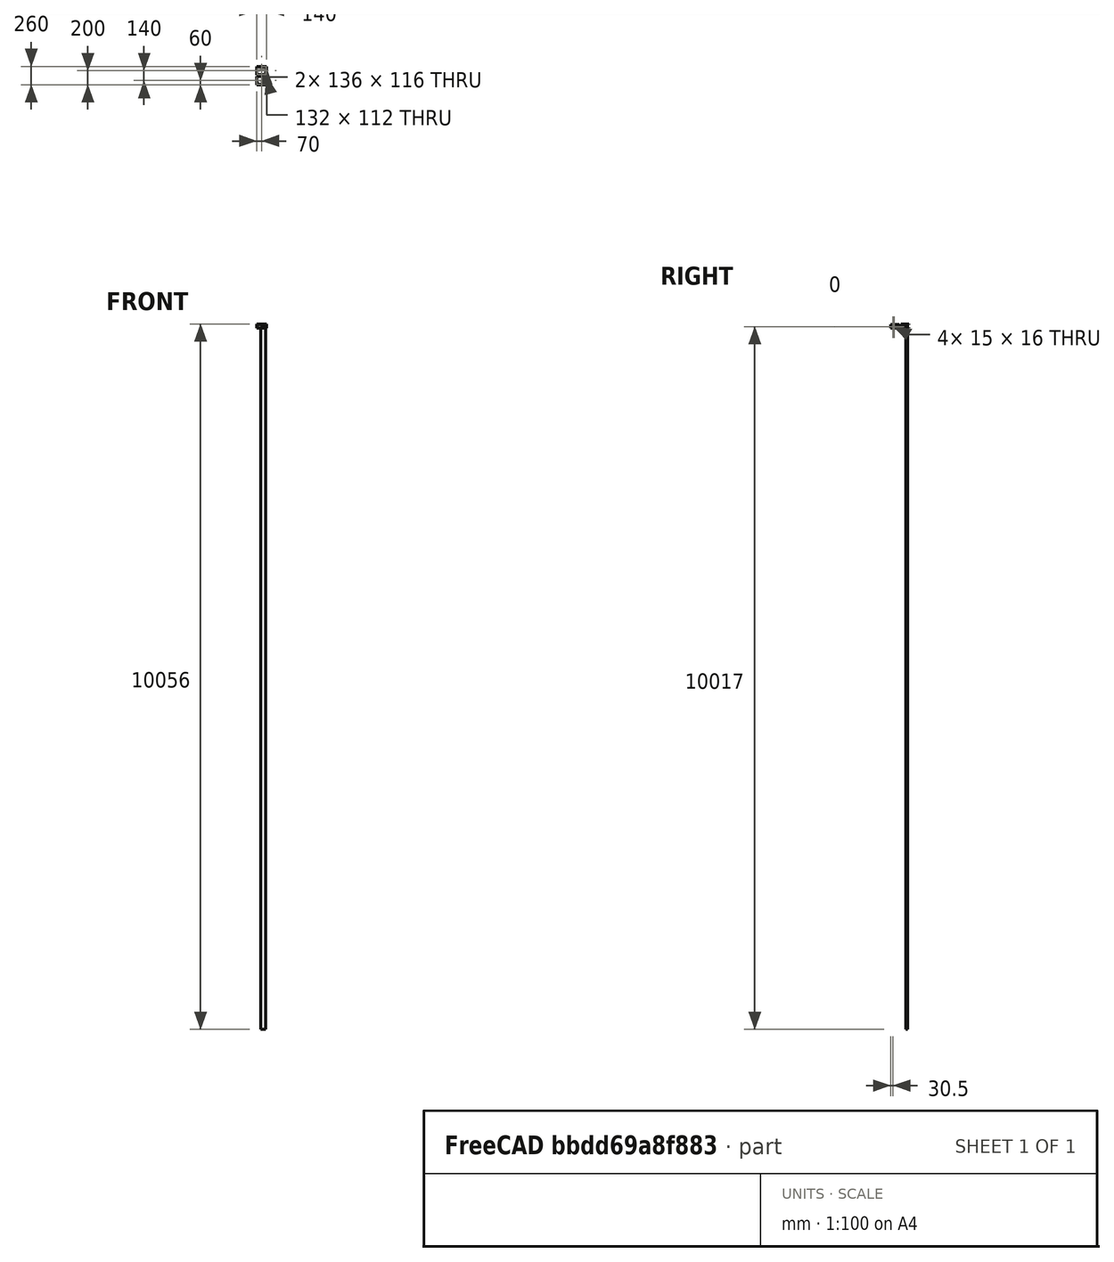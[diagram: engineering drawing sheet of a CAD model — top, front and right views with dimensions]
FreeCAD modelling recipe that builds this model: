
FCSTD DOCUMENT  (FreeCAD 0.15R4671 (Git))
Label: receptor
License: All rights reserved
LicenseURL: http://en.wikipedia.org/wiki/All_rights_reserved
objects: Sketcher::SketchObject×18, PartDesign::Pocket×11, PartDesign::Pad×7
note: 54 computed .brp shape members not serialized (recipe doc carries the construction recipe); baked Part::Feature solids carry a one-line shape summary decoded from their .brp

FEATURE [Sketcher::SketchObject] Sketch  label="full filled box"
  sketch-geometry (4):
    g0: LineSegment StartX=-70 StartY=60 StartZ=0 EndX=70 EndY=60 EndZ=0
    g1: LineSegment StartX=70 StartY=60 StartZ=0 EndX=70 EndY=-60 EndZ=0
    g2: LineSegment StartX=70 StartY=-60 StartZ=0 EndX=-70 EndY=-60 EndZ=0
    g3: LineSegment StartX=-70 StartY=-60 StartZ=0 EndX=-70 EndY=60 EndZ=0
  constraints (12):
    c: Coincident(g0,g1)
    c: Coincident(g1,g2)
    c: Coincident(g2,g3)
    c: Coincident(g3,g0)
    c: Horizontal(g0)
    c: Horizontal(g2)
    c: Vertical(g1)
    c: Vertical(g3)
    c: Symmetric(g0,g2,g-1)
    c: Symmetric(g0,g0,g-2)
    c: DistanceX(g0) = 140
    c: DistanceY(g3) = 120
FEATURE [PartDesign::Pad] Pad  label="full filled box001"
  Length = 50
  Length2 = 100
  Sketch = -> Sketch
  Type = 0
FEATURE [Sketcher::SketchObject] Sketch001  label="main hole box"
  Placement = pos=(0,0,50) rot=(0,0,1;0rad)
  Support = -> Pad [Face6]
  sketch-geometry (4):
    g0: LineSegment StartX=-68 StartY=58 StartZ=0 EndX=68 EndY=58 EndZ=0
    g1: LineSegment StartX=68 StartY=58 StartZ=0 EndX=68 EndY=-58 EndZ=0
    g2: LineSegment StartX=68 StartY=-58 StartZ=0 EndX=-68 EndY=-58 EndZ=0
    g3: LineSegment StartX=-68 StartY=-58 StartZ=0 EndX=-68 EndY=58 EndZ=0
  constraints (12):
    c: Coincident(g0,g1)
    c: Coincident(g1,g2)
    c: Coincident(g2,g3)
    c: Coincident(g3,g0)
    c: Horizontal(g0)
    c: Horizontal(g2)
    c: Vertical(g1)
    c: Vertical(g3)
    c: Symmetric(g0,g0,g-2)
    c: Symmetric(g0,g2,g-1)
    c: DistanceX(g0) = 136
    c: DistanceY(g3) = 116
FEATURE [PartDesign::Pocket] Pocket  label="main hole box001"
  Length = 48
  Sketch = -> Sketch001
  Type = 0
FEATURE [Sketcher::SketchObject] Sketch002
  Placement = pos=(0,0,2) rot=(0,0,1;0rad)
  Support = -> Pocket [Face11]
  sketch-geometry (8):
    g0: Circle CenterX=44 CenterY=-55 CenterZ=0 NormalX=0 NormalY=0 NormalZ=1 Radius=3
    g1: Circle CenterX=-14 CenterY=-55 CenterZ=0 NormalX=0 NormalY=0 NormalZ=1 Radius=3
    g2: Circle CenterX=44 CenterY=-6.5 CenterZ=0 NormalX=0 NormalY=0 NormalZ=1 Radius=3
    g3: Circle CenterX=-14 CenterY=-6.5 CenterZ=0 NormalX=0 NormalY=0 NormalZ=1 Radius=3
    g4: LineSegment [constr] StartX=-14 StartY=-6.5 StartZ=0 EndX=44 EndY=-6.5 EndZ=0
    g5: LineSegment [constr] StartX=-14 StartY=-6.5 StartZ=0 EndX=-14 EndY=-55 EndZ=0
    g6: LineSegment [constr] StartX=-14 StartY=-55 StartZ=0 EndX=44 EndY=-55 EndZ=0
    g7: LineSegment [constr] StartX=44 StartY=-6.5 StartZ=0 EndX=44 EndY=-55 EndZ=0
  constraints (20):
    c: Radius(g3) = 3
    c: Radius(g2) = 3
    c: Radius(g1) = 3
    c: Radius(g0) = 3
    c: DistanceY(g-1,g0) = -55
    c: DistanceX(g1,g0) = 58
    c: DistanceY(g0,g2) = 48.5
    c: DistanceX(g-1,g2) = 44
    c: Coincident(g4,g3)
    c: Coincident(g4,g2)
    c: Horizontal(g4)
    c: Coincident(g5,g3)
    c: Coincident(g5,g1)
    c: Vertical(g5)
    c: Coincident(g6,g1)
    c: Coincident(g6,g0)
    c: Coincident(g7,g2)
    c: Coincident(g7,g0)
    c: Vertical(g7)
    c: Horizontal(g6)
FEATURE [PartDesign::Pad] Pad001  label="legs raspberry fill"
  Length = 8
  Length2 = 100
  Sketch = -> Sketch002
  Type = 0
FEATURE [Sketcher::SketchObject] Sketch003
  Placement = pos=(0,0,10) rot=(0,0,1;0rad)
  Support = -> Pad001 [Face18]
  sketch-geometry (8):
    g0: Circle CenterX=-14 CenterY=-6.5 CenterZ=0 NormalX=0 NormalY=0 NormalZ=1 Radius=1.1
    g1: Circle CenterX=44 CenterY=-6.5 CenterZ=0 NormalX=0 NormalY=0 NormalZ=1 Radius=1.1
    g2: Circle CenterX=-14 CenterY=-55 CenterZ=0 NormalX=0 NormalY=0 NormalZ=1 Radius=1.1
    g3: Circle CenterX=44 CenterY=-55 CenterZ=0 NormalX=0 NormalY=0 NormalZ=1 Radius=1.1
    g4: LineSegment [constr] StartX=-14 StartY=-6.5 StartZ=0 EndX=-14 EndY=-55 EndZ=0
    g5: LineSegment [constr] StartX=-14 StartY=-6.5 StartZ=0 EndX=44 EndY=-6.5 EndZ=0
    g6: LineSegment [constr] StartX=44 StartY=-6.5 StartZ=0 EndX=44 EndY=-55 EndZ=0
    g7: LineSegment [constr] StartX=44 StartY=-55 StartZ=0 EndX=-14 EndY=-55 EndZ=0
  constraints (20):
    c: Radius(g0) = 1.1
    c: Radius(g3) = 1.1
    c: Radius(g2) = 1.1
    c: Radius(g1) = 1.1
    c: Coincident(g4,g0)
    c: Coincident(g4,g2)
    c: Vertical(g4)
    c: Coincident(g5,g0)
    c: Horizontal(g5)
    c: Coincident(g1,g5)
    c: Coincident(g6,g1)
    c: Coincident(g6,g3)
    c: Vertical(g6)
    c: Coincident(g7,g3)
    c: Coincident(g7,g2)
    c: Horizontal(g7)
    c: DistanceY(g-1,g2) = -55
    c: DistanceX(g-1,g1) = 44
    c: DistanceY(g0,g2) = -48.5
    c: DistanceX(g0,g1) = 58
FEATURE [PartDesign::Pocket] Pocket001  label="legs raspberry hole"
  Length = 8
  Sketch = -> Sketch003
  Type = 0
FEATURE [Sketcher::SketchObject] Sketch004
  Placement = pos=(70,0,0) rot=(0.57735,0.57735,0.57735;2.0944rad)
  Support = -> Pocket001 [Face3]
  sketch-geometry (12):
    g0: LineSegment StartX=-56 StartY=25 StartZ=0 EndX=-40 EndY=25 EndZ=0
    g1: LineSegment StartX=-40 StartY=25 StartZ=0 EndX=-40 EndY=11 EndZ=0
    g2: LineSegment StartX=-40 StartY=11 StartZ=0 EndX=-56 EndY=11 EndZ=0
    g3: LineSegment StartX=-56 StartY=11 StartZ=0 EndX=-56 EndY=25 EndZ=0
    g4: LineSegment StartX=-37 StartY=27 StartZ=0 EndX=-22 EndY=27 EndZ=0
    g5: LineSegment StartX=-22 StartY=27 StartZ=0 EndX=-22 EndY=11 EndZ=0
    g6: LineSegment StartX=-22 StartY=11 StartZ=0 EndX=-37 EndY=11 EndZ=0
    g7: LineSegment StartX=-37 StartY=11 StartZ=0 EndX=-37 EndY=27 EndZ=0
    g8: LineSegment StartX=-19 StartY=27 StartZ=0 EndX=-4 EndY=27 EndZ=0
    g9: LineSegment StartX=-4 StartY=27 StartZ=0 EndX=-4 EndY=11 EndZ=0
    g10: LineSegment StartX=-4 StartY=11 StartZ=0 EndX=-19 EndY=11 EndZ=0
    g11: LineSegment StartX=-19 StartY=11 StartZ=0 EndX=-19 EndY=27 EndZ=0
  constraints (36):
    c: Coincident(g0,g1)
    c: Coincident(g1,g2)
    c: Coincident(g2,g3)
    c: Coincident(g3,g0)
    c: Horizontal(g0)
    c: Horizontal(g2)
    c: Vertical(g1)
    c: Vertical(g3)
    c: Coincident(g4,g5)
    c: Coincident(g5,g6)
    c: Coincident(g6,g7)
    c: Coincident(g7,g4)
    c: Horizontal(g4)
    c: Horizontal(g6)
    c: Vertical(g5)
    c: Vertical(g7)
    c: Coincident(g8,g9)
    c: Coincident(g9,g10)
    c: Coincident(g10,g11)
    c: Coincident(g11,g8)
    c: Horizontal(g8)
    c: Horizontal(g10)
    c: Vertical(g9)
    c: Vertical(g11)
    c: DistanceX(g-1,g2) = -56
    c: DistanceX(g2) = -16
    c: DistanceY(g3) = 14
    c: DistanceY(g-1,g1) = 11
    c: DistanceX(g6,g1) = -3
    c: DistanceY(g-1,g6) = 11
    c: DistanceY(g-1,g10) = 11
    c: DistanceX(g6) = -15
    c: DistanceY(g7) = 16
    c: DistanceY(g11) = 16
    c: DistanceX(g10) = -15
    c: DistanceX(g10,g5) = -3
FEATURE [PartDesign::Pocket] Pocket002  label="holes raspberry periphericals"
  Length = 5
  Sketch = -> Sketch004
  Type = 0
FEATURE [Sketcher::SketchObject] Sketch005
  Placement = pos=(0,-60,0) rot=(1,0,0;1.5708rad)
  Support = -> Pocket002 [Face6]
  sketch-geometry (9):
    g0: Circle CenterX=37 CenterY=14 CenterZ=0 NormalX=0 NormalY=0 NormalZ=1 Radius=3
    g1: LineSegment StartX=8 StartY=17 StartZ=0 EndX=23 EndY=17 EndZ=0
    g2: LineSegment StartX=23 StartY=17 StartZ=0 EndX=23 EndY=11 EndZ=0
    g3: LineSegment StartX=23 StartY=11 StartZ=0 EndX=8 EndY=11 EndZ=0
    g4: LineSegment StartX=8 StartY=11 StartZ=0 EndX=8 EndY=17 EndZ=0
    g5: LineSegment StartX=-10 StartY=14 StartZ=0 EndX=-2 EndY=14 EndZ=0
    g6: LineSegment StartX=-2 StartY=14 StartZ=0 EndX=-2 EndY=11 EndZ=0
    g7: LineSegment StartX=-2 StartY=11 StartZ=0 EndX=-10 EndY=11 EndZ=0
    g8: LineSegment StartX=-10 StartY=11 StartZ=0 EndX=-10 EndY=14 EndZ=0
  constraints (27):
    c: Coincident(g1,g2)
    c: Coincident(g2,g3)
    c: Coincident(g3,g4)
    c: Coincident(g4,g1)
    c: Horizontal(g1)
    c: Horizontal(g3)
    c: Vertical(g2)
    c: Vertical(g4)
    c: Coincident(g5,g6)
    c: Coincident(g6,g7)
    c: Coincident(g7,g8)
    c: Coincident(g8,g5)
    c: Horizontal(g5)
    c: Horizontal(g7)
    c: Vertical(g6)
    c: Vertical(g8)
    c: Radius(g0) = 3
    c: DistanceX(g1) = 15
    c: DistanceX(g5) = 8
    c: DistanceY(g8) = 3
    c: DistanceY(g4) = 6
    c: DistanceY(g-1,g6) = 11
    c: DistanceY(g-1,g2) = 11
    c: DistanceY(g-1,g0) = 14
    c: DistanceX(g-1,g7) = -10
    c: DistanceX(g6,g3) = 10
    c: DistanceX(g2,g0) = 14
FEATURE [PartDesign::Pocket] Pocket003  label="holes raspberry power"
  Length = 5
  Sketch = -> Sketch005
  Type = 0
FEATURE [Sketcher::SketchObject] Sketch006
  Placement = pos=(0,0,2) rot=(0,0,1;0rad)
  Support = -> Pocket003 [Face32]
  sketch-geometry (3):
    g0: Circle CenterX=-59 CenterY=-30 CenterZ=0 NormalX=0 NormalY=0 NormalZ=1 Radius=3
    g1: Circle CenterX=-46 CenterY=-30 CenterZ=0 NormalX=0 NormalY=0 NormalZ=1 Radius=3
    g2: LineSegment [constr] StartX=-59 StartY=-30 StartZ=0 EndX=-46 EndY=-30 EndZ=0
  constraints (8):
    c: Radius(g1) = 3
    c: Equal(g1,g0)
    c: Coincident(g2,g1)
    c: Coincident(g2,g0)
    c: Parallel(g2,g-1)
    c: DistanceX(g-1,g0) = -59
    c: DistanceX(g2) = 13
    c: DistanceY(g-1,g1) = -30
FEATURE [PartDesign::Pad] Pad002  label="legs lora fill"
  Length = 30
  Length2 = 100
  Sketch = -> Sketch006
  Type = 0
FEATURE [Sketcher::SketchObject] Sketch007
  Placement = pos=(0,0,32) rot=(0,0,1;0rad)
  Support = -> Pad002 [Face42]
  sketch-geometry (3):
    g0: Circle CenterX=-59 CenterY=-30 CenterZ=0 NormalX=0 NormalY=0 NormalZ=1 Radius=1.1
    g1: Circle CenterX=-46 CenterY=-30 CenterZ=0 NormalX=0 NormalY=0 NormalZ=1 Radius=1.1
    g2: LineSegment [constr] StartX=-59 StartY=-30 StartZ=0 EndX=-46 EndY=-30 EndZ=0
  constraints (8):
    c: Radius(g1) = 1.1
    c: Equal(g1,g0)
    c: Coincident(g2,g1)
    c: Parallel(g2,g-1)
    c: Coincident(g0,g2)
    c: DistanceX(g2) = 13
    c: DistanceX(g-1,g0) = -59
    c: DistanceY(g-1,g1) = -30
FEATURE [PartDesign::Pocket] Pocket004  label="legs lora hole"
  Length = 25
  Sketch = -> Sketch007
  Type = 0
FEATURE [Sketcher::SketchObject] Sketch008
  Placement = pos=(-70,0,0) rot=(0.57735,-0.57735,-0.57735;2.0944rad)
  Support = -> Pocket004 [Face2]
  sketch-geometry (1):
    g0: Circle CenterX=30 CenterY=38 CenterZ=0 NormalX=0 NormalY=0 NormalZ=1 Radius=4
  constraints (3):
    c: Radius(g0) = 4
    c: DistanceX(g-1,g0) = 30
    c: DistanceY(g-1,g0) = 38
FEATURE [PartDesign::Pocket] Pocket005  label="pocket lora antenna"
  Length = 5
  Sketch = -> Sketch008
  Type = 0
FEATURE [Sketcher::SketchObject] Sketch009  label="top 1"
  Placement = pos=(0,0,0) rot=(1,0,0;3.14159rad)
  Support = -> Pocket005 [Face4]
  sketch-geometry (4):
    g0: LineSegment StartX=-70 StartY=-80 StartZ=0 EndX=70 EndY=-80 EndZ=0
    g1: LineSegment StartX=70 StartY=-80 StartZ=0 EndX=70 EndY=-200 EndZ=0
    g2: LineSegment StartX=70 StartY=-200 StartZ=0 EndX=-70 EndY=-200 EndZ=0
    g3: LineSegment StartX=-70 StartY=-200 StartZ=0 EndX=-70 EndY=-80 EndZ=0
  constraints (12):
    c: Coincident(g0,g1)
    c: Coincident(g1,g2)
    c: Coincident(g2,g3)
    c: Coincident(g3,g0)
    c: Horizontal(g0)
    c: Horizontal(g2)
    c: Vertical(g1)
    c: Vertical(g3)
    c: DistanceY(g3) = 120
    c: DistanceX(g2) = -140
    c: DistanceY(g-1,g0) = -80
    c: Symmetric(g0,g0,g-2)
FEATURE [PartDesign::Pad] Pad003  label="top1"
  Length = 2
  Length2 = 100
  Sketch = -> Sketch009
  Type = 0
FEATURE [Sketcher::SketchObject] Sketch010
  Placement = pos=(0,0,50) rot=(0,0,1;0rad)
  Support = -> Pad003 [Face5]
  sketch-geometry (4):
    g0: LineSegment StartX=-68 StartY=198 StartZ=0 EndX=68 EndY=198 EndZ=0
    g1: LineSegment StartX=68 StartY=198 StartZ=0 EndX=68 EndY=82 EndZ=0
    g2: LineSegment StartX=68 StartY=82 StartZ=0 EndX=-68 EndY=82 EndZ=0
    g3: LineSegment StartX=-68 StartY=82 StartZ=0 EndX=-68 EndY=198 EndZ=0
  constraints (12):
    c: Coincident(g0,g1)
    c: Coincident(g1,g2)
    c: Coincident(g2,g3)
    c: Coincident(g3,g0)
    c: Horizontal(g0)
    c: Horizontal(g2)
    c: Vertical(g1)
    c: Vertical(g3)
    c: DistanceX(g0) = 136
    c: DistanceY(g3) = 116
    c: Symmetric(g0,g0,g-2)
    c: DistanceY(g-1,g1) = 82
FEATURE [PartDesign::Pad] Pad004  label="top2"
  Length = 8
  Length2 = 100
  Sketch = -> Sketch010
  Type = 0
FEATURE [Sketcher::SketchObject] Sketch011
  Placement = pos=(0,0,8) rot=(0,0,1;0rad)
  Support = -> Pad004 [Face11]
  sketch-geometry (4):
    g0: LineSegment StartX=-66 StartY=196 StartZ=0 EndX=66 EndY=196 EndZ=0
    g1: LineSegment StartX=66 StartY=196 StartZ=0 EndX=66 EndY=84 EndZ=0
    g2: LineSegment StartX=66 StartY=84 StartZ=0 EndX=-66 EndY=84 EndZ=0
    g3: LineSegment StartX=-66 StartY=84 StartZ=0 EndX=-66 EndY=196 EndZ=0
  constraints (12):
    c: Coincident(g0,g1)
    c: Coincident(g1,g2)
    c: Coincident(g2,g3)
    c: Coincident(g3,g0)
    c: Horizontal(g0)
    c: Horizontal(g2)
    c: Vertical(g1)
    c: Vertical(g3)
    c: DistanceX(g0) = 132
    c: DistanceY(g3) = 112
    c: Symmetric(g0,g0,g-2)
    c: DistanceY(g-1,g1) = 84
FEATURE [PartDesign::Pocket] Pocket006  label="top3"
  Length = 6
  Sketch = -> Sketch011
  Type = 0
FEATURE [Sketcher::SketchObject] Sketch012
  Placement = pos=(0,0,2) rot=(0,0,1;0rad)
  Support = -> Pocket006 [Face16]
  sketch-geometry (8):
    g0: Circle CenterX=60 CenterY=185 CenterZ=0 NormalX=0 NormalY=0 NormalZ=1 Radius=3
    g1: Circle CenterX=-15 CenterY=185 CenterZ=0 NormalX=0 NormalY=0 NormalZ=1 Radius=3
    g2: Circle CenterX=60 CenterY=154 CenterZ=0 NormalX=0 NormalY=0 NormalZ=1 Radius=3
    g3: Circle CenterX=-15 CenterY=154 CenterZ=0 NormalX=0 NormalY=0 NormalZ=1 Radius=3
    g4: LineSegment [constr] StartX=-15 StartY=185 StartZ=0 EndX=60 EndY=185 EndZ=0
    g5: LineSegment [constr] StartX=-15 StartY=154 StartZ=0 EndX=-15 EndY=185 EndZ=0
    g6: LineSegment [constr] StartX=60 StartY=154 StartZ=0 EndX=-15 EndY=154 EndZ=0
    g7: LineSegment [constr] StartX=60 StartY=185 StartZ=0 EndX=60 EndY=154 EndZ=0
  constraints (20):
    c: Radius(g3) = 3
    c: Equal(g3,g1)
    c: Equal(g3,g2)
    c: Equal(g3,g0)
    c: Coincident(g4,g1)
    c: Coincident(g4,g0)
    c: Horizontal(g4)
    c: Coincident(g5,g1)
    c: Coincident(g7,g0)
    c: Coincident(g7,g2)
    c: Horizontal(g6)
    c: Vertical(g5)
    c: Vertical(g7)
    c: Coincident(g6,g2)
    c: Coincident(g5,g3)
    c: Coincident(g6,g3)
    c: DistanceX(g4) = 75
    c: DistanceY(g5) = 31
    c: DistanceX(g-1,g0) = 60
    c: DistanceY(g-1,g0) = 185
FEATURE [PartDesign::Pad] Pad005  label="legs led fill"
  Length = 6
  Length2 = 100
  Sketch = -> Sketch012
  Type = 0
FEATURE [Sketcher::SketchObject] Sketch013
  Placement = pos=(0,0,8) rot=(0,0,1;0rad)
  Support = -> Pad005 [Face23]
  sketch-geometry (8):
    g0: Circle CenterX=-15 CenterY=185 CenterZ=0 NormalX=0 NormalY=0 NormalZ=1 Radius=1.1
    g1: Circle CenterX=60 CenterY=185 CenterZ=0 NormalX=0 NormalY=0 NormalZ=1 Radius=1.1
    g2: Circle CenterX=-15 CenterY=154 CenterZ=0 NormalX=0 NormalY=0 NormalZ=1 Radius=1.1
    g3: Circle CenterX=60 CenterY=154 CenterZ=0 NormalX=0 NormalY=0 NormalZ=1 Radius=1.1
    g4: LineSegment [constr] StartX=-15 StartY=185 StartZ=0 EndX=60 EndY=185 EndZ=0
    g5: LineSegment [constr] StartX=60 StartY=185 StartZ=0 EndX=60 EndY=154 EndZ=0
    g6: LineSegment [constr] StartX=60 StartY=154 StartZ=0 EndX=-15 EndY=154 EndZ=0
    g7: LineSegment [constr] StartX=-15 StartY=154 StartZ=0 EndX=-15 EndY=185 EndZ=0
  constraints (20):
    c: Radius(g3) = 1.1
    c: Equal(g3,g2)
    c: Equal(g3,g0)
    c: Equal(g3,g1)
    c: Coincident(g4,g5)
    c: Coincident(g5,g6)
    c: Coincident(g6,g7)
    c: Coincident(g7,g4)
    c: Horizontal(g4)
    c: Horizontal(g6)
    c: Vertical(g5)
    c: Vertical(g7)
    c: Coincident(g0,g4)
    c: Coincident(g2,g6)
    c: Coincident(g3,g5)
    c: Coincident(g4,g1)
    c: DistanceX(g4) = 75
    c: DistanceY(g7) = 31
    c: DistanceY(g-1,g1) = 185
    c: DistanceX(g-1,g1) = 60
FEATURE [PartDesign::Pocket] Pocket007  label="legs led hole"
  Length = 6
  Sketch = -> Sketch013
  Type = 0
FEATURE [Sketcher::SketchObject] Sketch014
  Placement = pos=(0,0,2) rot=(0,0,1;0rad)
  Support = -> Pocket007 [Face16]
  sketch-geometry (4):
    g0: LineSegment StartX=-13 StartY=181 StartZ=0 EndX=58 EndY=181 EndZ=0
    g1: LineSegment StartX=58 StartY=181 StartZ=0 EndX=58 EndY=155 EndZ=0
    g2: LineSegment StartX=58 StartY=155 StartZ=0 EndX=-13 EndY=155 EndZ=0
    g3: LineSegment StartX=-13 StartY=155 StartZ=0 EndX=-13 EndY=181 EndZ=0
  constraints (12):
    c: Coincident(g0,g1)
    c: Coincident(g1,g2)
    c: Coincident(g2,g3)
    c: Coincident(g3,g0)
    c: Horizontal(g0)
    c: Horizontal(g2)
    c: Vertical(g1)
    c: Vertical(g3)
    c: DistanceX(g0) = 71
    c: DistanceY(g3) = 26
    c: DistanceX(g-1,g0) = 58
    c: DistanceY(g-1,g0) = 181
FEATURE [PartDesign::Pocket] Pocket008  label="screen hole"
  Length = 5
  Sketch = -> Sketch014
  Type = 1
FEATURE [Sketcher::SketchObject] Sketch015
  Placement = pos=(0,0,2) rot=(0,0,1;0rad)
  Support = -> Pocket008 [Face17]
  sketch-geometry (3):
    g0: Circle CenterX=-35 CenterY=185 CenterZ=0 NormalX=0 NormalY=0 NormalZ=1 Radius=3
    g1: Circle CenterX=-35 CenterY=142 CenterZ=0 NormalX=0 NormalY=0 NormalZ=1 Radius=3
    g2: LineSegment [constr] StartX=-35 StartY=185 StartZ=0 EndX=-35 EndY=142 EndZ=0
  constraints (8):
    c: Radius(g0) = 3
    c: Equal(g0,g1)
    c: Coincident(g2,g0)
    c: Coincident(g2,g1)
    c: Vertical(g2)
    c: DistanceY(g2) = -43
    c: DistanceX(g-1,g0) = -35
    c: DistanceY(g-1,g0) = 185
FEATURE [PartDesign::Pad] Pad006
  Length = 6
  Length2 = 100
  Sketch = -> Sketch015
  Type = 0
FEATURE [Sketcher::SketchObject] Sketch016
  Placement = pos=(0,0,8) rot=(0,0,1;0rad)
  Support = -> Pad006 [Face30]
  sketch-geometry (3):
    g0: Circle CenterX=-35 CenterY=185 CenterZ=0 NormalX=0 NormalY=0 NormalZ=1 Radius=1.1
    g1: Circle CenterX=-35 CenterY=142 CenterZ=0 NormalX=0 NormalY=0 NormalZ=1 Radius=1.1
    g2: LineSegment [constr] StartX=-35 StartY=185 StartZ=0 EndX=-35 EndY=142 EndZ=0
  constraints (8):
    c: Radius(g1) = 1.1
    c: Equal(g1,g0)
    c: Coincident(g2,g0)
    c: Coincident(g2,g1)
    c: Vertical(g2)
    c: DistanceY(g2) = -43
    c: DistanceX(g-1,g0) = -35
    c: DistanceY(g-1,g0) = 185
FEATURE [PartDesign::Pocket] Pocket009
  Length = 6
  Sketch = -> Sketch016
  Type = 0
FEATURE [Sketcher::SketchObject] Sketch017
  Placement = pos=(0,0,2) rot=(0,0,1;0rad)
  Support = -> Pocket009 [Face17]
  sketch-geometry (4):
    g0: Circle CenterX=-27 CenterY=177 CenterZ=0 NormalX=0 NormalY=0 NormalZ=1 Radius=2
    g1: Circle CenterX=-27 CenterY=166.5 CenterZ=0 NormalX=0 NormalY=0 NormalZ=1 Radius=2
    g2: Circle CenterX=-27 CenterY=149 CenterZ=0 NormalX=0 NormalY=0 NormalZ=1 Radius=6
    g3: LineSegment [constr] StartX=-27 StartY=177 StartZ=0 EndX=-27 EndY=149 EndZ=0
  constraints (11):
    c: Vertical(g3)
    c: Coincident(g2,g3)
    c: PointOnObject(g1,g3)
    c: Coincident(g0,g3)
    c: Radius(g0) = 2
    c: Equal(g0,g1)
    c: Radius(g2) = 6
    c: DistanceY(g0,g1) = -10.5
    c: DistanceY(g1,g2) = -17.5
    c: DistanceX(g-1,g0) = -27
    c: DistanceY(g-1,g0) = 177
FEATURE [PartDesign::Pocket] Pocket010
  Length = 5
  Sketch = -> Sketch017
  Type = 0
